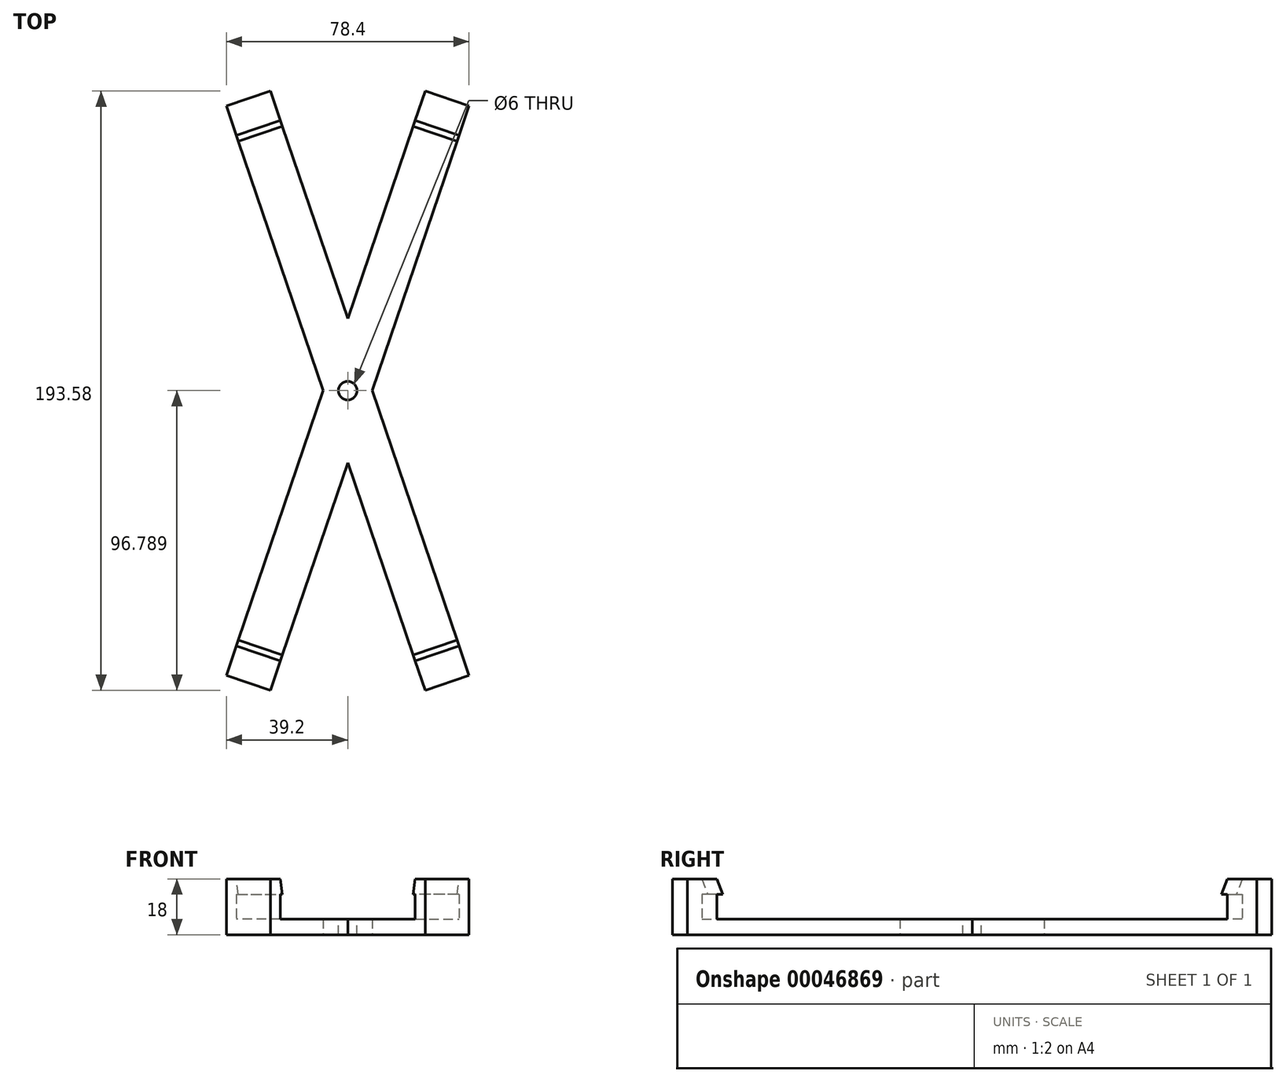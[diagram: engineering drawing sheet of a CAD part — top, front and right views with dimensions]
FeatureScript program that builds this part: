
annotation { "Feature Type Name" : "Feature", "Feature Type Description" : "" }
export const myFeature = defineFeature(function(context is Context, id is Id, definition is map)
    precondition{}
    {
        {
            var Q0;
            Q0=qCreatedBy(makeId("Top.planeOp"),FACE);
            var sketch = newSketch(context, id + "F6", { "sketchPlane" : qUnion([Q0])});
            skLineSegment(sketch, "E0", {"start": v(7.92, -23.3) * mm, "end": v(39.2, 68.67) * mm});
            skLineSegment(sketch, "E1", {"start": v(39.2, 68.67) * mm, "end": v(25, 73.5) * mm});
            skLineSegment(sketch, "E2", {"start": v(25, 73.5) * mm, "end": v(0, 0) * mm});
            skLineSegment(sketch, "E3", {"start": v(7.92, -23.3) * mm, "end": v(0, -23.3) * mm});
            skLineSegment(sketch, "E4", {"start": v(0, 0) * mm, "end": v(0, -23.3) * mm});
            skLineSegment(sketch, "E5", {"start": v(21.78, 64.03) * mm, "end": v(35.98, 59.2) * mm});
            skSolve(sketch);
        }
        {
            var Q0;
            {var subQ9=sQuery(id+"F6.wireOp",EDGE,"E5");Q0=makeQuery(id+"F6.imprint","IMPRINT",FACE,{"disambiguationData":[TD([[makeQuery(id+"F6.imprint","IMPRINT",EDGE,{"derivedFrom":subQ9}),-1.0]])]});}
            extrude(context, id + "F7", {"entities" : qUnion([Q0]), "depth" : 5 * mm});
        }
        {
            var Q0;
            {var subQ1=sQuery(id+"F6.wireOp",EDGE,"be22bed6-d2ba-4a80-a1e6-ca4f79abf1950.MirrorCS");Q0=makeQuery(id+"F6.imprint","IMPRINT",FACE,{"disambiguationData":[TD([[makeQuery(id+"F6.imprint","IMPRINT",EDGE,{"derivedFrom":subQ1}),-1.0]])]});}
            var Q1;
            {var subQ2=sQuery(id+"F6.wireOp",EDGE,"E1");Q1=makeQuery(id+"F6.imprint","IMPRINT",FACE,{"disambiguationData":[TD([[makeQuery(id+"F6.imprint","IMPRINT",EDGE,{"derivedFrom":subQ2}),1.0]])]});}
            var Q2;
            {var subQ2=sQuery(id+"F6.wireOp",EDGE,"cad02350-30c8-41e9-b1a9-362eb5ac6a3d0.MirrorCS");Q2=makeQuery(id+"F6.imprint","IMPRINT",FACE,{"disambiguationData":[TD([[makeQuery(id+"F6.imprint","IMPRINT",EDGE,{"derivedFrom":subQ2}),-1.0]])]});}
            var Q3;
            {var subQ1=sQuery(id+"F6.wireOp",EDGE,"fa579f65-90d0-4518-987f-1a988788fe310.MirrorCS");Q3=makeQuery(id+"F6.imprint","IMPRINT",FACE,{"disambiguationData":[TD([[makeQuery(id+"F6.imprint","IMPRINT",EDGE,{"derivedFrom":subQ1}),1.0]])]});}
            extrude(context, id + "F0", {"entities" : qUnion([Q0, Q1, Q2, Q3]), "operationType" : NewBodyOperationType.ADD, "depth" : 18 * mm});
        }
        {
            var Q0;
            {var subQ0=sQuery(id+"F6.wireOp",EDGE,"E2");Q0=makeQuery(id+"F0.boolean.opBoolean","MERGE",FACE,{"derivedFrom":[makeQuery(id+"F7.opExtrude","SWEPT_FACE",FACE,{"disambiguationData":[OSD([subQ0])]}),makeQuery(id+"F0.opExtrude","SWEPT_FACE",FACE,{"disambiguationData":[OSD([subQ0])]})]});}
            var sketch = newSketch(context, id + "F1", { "sketchPlane" : qUnion([Q0])});
            skLineSegment(sketch, "E6", {"start": v(-67.64, 18) * mm, "end": v(-65.64, 13) * mm});
            skLineSegment(sketch, "E7", {"start": v(-65.64, 13) * mm, "end": v(-67.64, 13) * mm});
            skLineSegment(sketch, "E8", {"start": v(-67.64, 18) * mm, "end": v(-67.64, 13) * mm});
            skSolve(sketch);
        }
        {
            var Q0;
            Q0=makeQuery(id+"F1.imprint","IMPRINT",FACE,{"disambiguationData":[TD([[makeQuery(id+"F1.imprint","IMPRINT",EDGE,{"derivedFrom":sQuery(id+"F1.wireOp",EDGE,"E6")}),-1.0]])]});
            var Q1;
            {var subQ0=sQuery(id+"F6.wireOp",EDGE,"E0");Q1=makeQuery(id+"F0.boolean.opBoolean","MERGE",FACE,{"derivedFrom":[makeQuery(id+"F7.opExtrude","SWEPT_FACE",FACE,{"disambiguationData":[OSD([subQ0])]}),makeQuery(id+"F0.opExtrude","SWEPT_FACE",FACE,{"disambiguationData":[OSD([subQ0])]})]});}
            extrude(context, id + "F2", {"entities" : qUnion([Q0]), "operationType" : NewBodyOperationType.ADD, "endBound" : BoundingType.UP_TO_SURFACE, "oppositeDirection" : true, "endBoundEntityFace" : qUnion([Q1]), "depth" : 25 * mm});
        }
        {
            var Q0;
            Q0=makeQuery(id+"F7.opExtrude","SWEPT_BODY",BODY,{"disambiguationData":[OSD([sQuery(id+"F6.wireOp",EDGE,"E0"),sQuery(id+"F6.wireOp",EDGE,"E2"),sQuery(id+"F6.wireOp",EDGE,"E3"),sQuery(id+"F6.wireOp",EDGE,"E4"),sQuery(id+"F6.wireOp",EDGE,"E5")])]});
            var Q1;
            Q1=makeQuery(id+"F7.opExtrude","SWEPT_FACE",FACE,{"disambiguationData":[OSD([sQuery(id+"F6.wireOp",EDGE,"E4")])]});
            mirror(context, id + "F3", {"operationType" : NewBodyOperationType.ADD, "entities" : qUnion([Q0]), "mirrorPlane" : qUnion([Q1])});
        }
        {
            var Q0;
            Q0=makeQuery(id+"F7.opExtrude","SWEPT_BODY",BODY,{"disambiguationData":[OSD([sQuery(id+"F6.wireOp",EDGE,"E0"),sQuery(id+"F6.wireOp",EDGE,"E2"),sQuery(id+"F6.wireOp",EDGE,"E3"),sQuery(id+"F6.wireOp",EDGE,"E4"),sQuery(id+"F6.wireOp",EDGE,"E5")])]});
            var Q1;
            {var subQ0=makeQuery(id+"F7.opExtrude","SWEPT_FACE",FACE,{"disambiguationData":[OSD([sQuery(id+"F6.wireOp",EDGE,"E3")])]});Q1=makeQuery(id+"F3.boolean.opBoolean","MERGE",FACE,{"derivedFrom":[subQ0,makeQuery(id+"F3.opPattern","COPY",FACE,{"derivedFrom":subQ0,"instanceName":"1"})]});}
            mirror(context, id + "F4", {"operationType" : NewBodyOperationType.ADD, "entities" : qUnion([Q0]), "mirrorPlane" : qUnion([Q1])});
        }
        {
            var Q0;
            {var subQ0=makeQuery(id+"F7.opExtrude","CAP_FACE",FACE,{"disambiguationData":[OSD([sQuery(id+"F6.wireOp",EDGE,"E0"),sQuery(id+"F6.wireOp",EDGE,"E2"),sQuery(id+"F6.wireOp",EDGE,"E3"),sQuery(id+"F6.wireOp",EDGE,"E4"),sQuery(id+"F6.wireOp",EDGE,"E5")])],"isStart":false});var subQ1=makeQuery(id+"F3.boolean.opBoolean","MERGE",FACE,{"derivedFrom":[subQ0,makeQuery(id+"F3.opPattern","COPY",FACE,{"derivedFrom":subQ0,"instanceName":"1"})]});Q0=makeQuery(id+"F4.boolean.opBoolean","MERGE",FACE,{"derivedFrom":[subQ1,makeQuery(id+"F4.opPattern","COPY",FACE,{"derivedFrom":subQ1,"instanceName":"1"})]});}
            var sketch = newSketch(context, id + "F5", { "sketchPlane" : qUnion([Q0])});
            skCircle(sketch, "E9", {"center": v(0, -23.3) * mm, "radius": 3 * mm});
            skSolve(sketch);
        }
        {
            var Q0;
            Q0=makeQuery(id+"F5.imprint","IMPRINT",FACE,{"disambiguationData":[TD([[makeQuery(id+"F5.imprint","IMPRINT",EDGE,{"derivedFrom":sQuery(id+"F5.wireOp",EDGE,"E9")}),1.0]])]});
            extrude(context, id + "F8", {"entities" : qUnion([Q0]), "operationType" : NewBodyOperationType.REMOVE, "oppositeDirection" : true, "depth" : 25 * mm});
        }
    });
